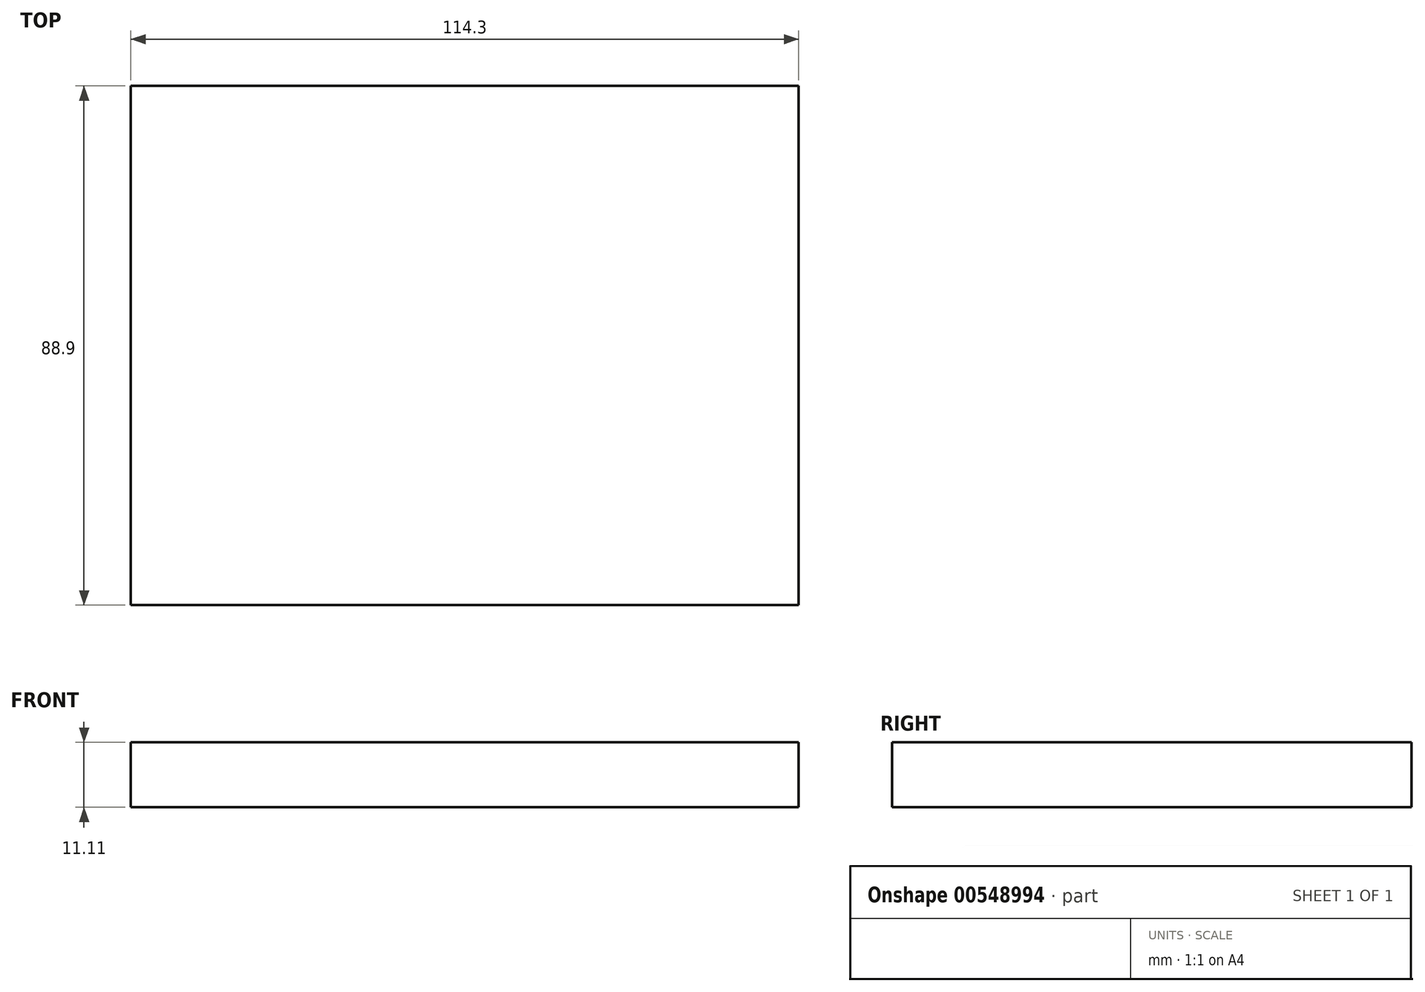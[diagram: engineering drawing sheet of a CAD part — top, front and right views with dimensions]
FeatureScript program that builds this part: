
annotation { "Feature Type Name" : "Feature", "Feature Type Description" : "" }
export const myFeature = defineFeature(function(context is Context, id is Id, definition is map)
    precondition{}
    {
        {
            var Q0;
            Q0=qCreatedBy(makeId("Top.planeOp"),FACE);
            var sketch = newSketch(context, id + "F0", { "sketchPlane" : qUnion([Q0])});
            skLineSegment(sketch, "E0.bottom", {"start": v(57.15, -44.45) * mm, "end": v(-57.15, -44.45) * mm});
            skLineSegment(sketch, "E0.top", {"start": v(57.15, 44.45) * mm, "end": v(-57.15, 44.45) * mm});
            skLineSegment(sketch, "E0.left", {"start": v(57.15, -44.45) * mm, "end": v(57.15, 44.45) * mm});
            skLineSegment(sketch, "E0.right", {"start": v(-57.15, -44.45) * mm, "end": v(-57.15, 44.45) * mm});
            skPoint(sketch, "E0.middle", {"position": v(0, 0) * mm});
            skSolve(sketch);
        }
        {
            var Q0;
            Q0 = qSketchRegion(id + "F0", true);
            extrude(context, id + "F1", {"entities" : qUnion([Q0]), "depth" : 11.1 * mm, "offsetDistance" : 25.4 * mm});
        }
    });
